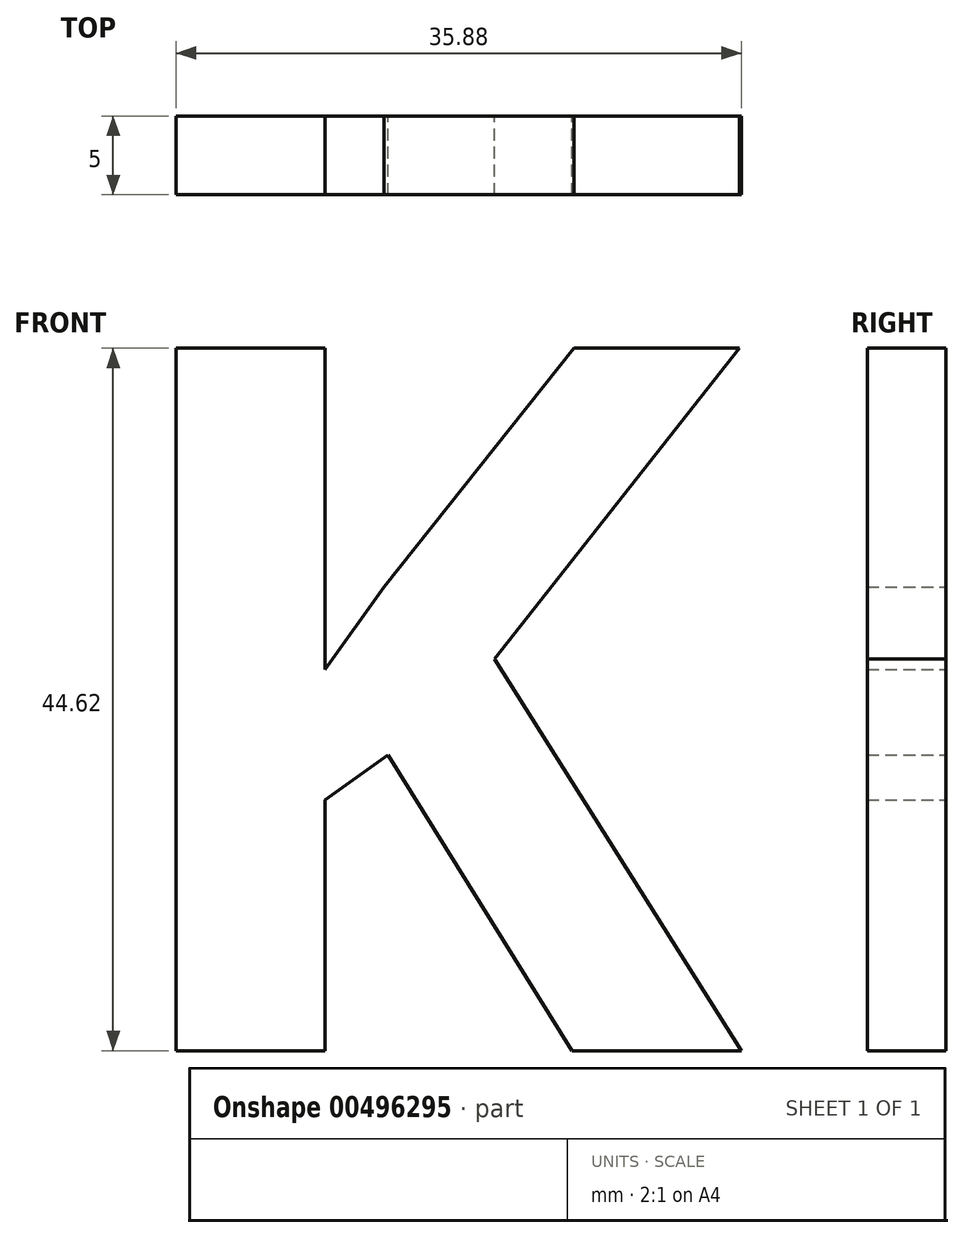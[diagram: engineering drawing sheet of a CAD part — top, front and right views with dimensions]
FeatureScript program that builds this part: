
annotation { "Feature Type Name" : "Feature", "Feature Type Description" : "" }
export const myFeature = defineFeature(function(context is Context, id is Id, definition is map)
    precondition{}
    {
        {
            var Q0;
            Q0=qCreatedBy(makeId("Front.planeOp"),FACE);
            var sketch = newSketch(context, id + "F0", { "sketchPlane" : qUnion([Q0])});
            skText(sketch, "E0", { "text": "K", "fontName": "OpenSans-Bold.ttf"});
            const initialGuessF0  = {"E0": [-0.06375, 0.01452, 1, 0, 0.045]};
            skSetInitialGuess(sketch, initialGuessF0);
            skSolve(sketch);
        }
        {
            var Q0;
            Q0=makeQuery(id+"F0.imprint","IMPRINT",FACE,{"disambiguationData":[TD([[makeQuery(id+"F0.imprint","IMPRINT",EDGE,{"derivedFrom":sQuery(id+"F0.wireOp",EDGE,"E0.sketch_text.stroke-0")}),-1.0]])]});
            extrude(context, id + "F1", {"entities" : qUnion([Q0]), "depth" : 5 * mm});
        }
    });
